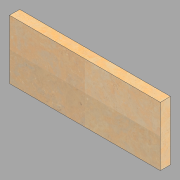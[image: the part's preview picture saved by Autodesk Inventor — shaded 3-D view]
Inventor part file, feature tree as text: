
AUTODESK INVENTOR PART (.ipt)
format: ipt  version: 2022.1 (Build 261234020, 234B)  size: 108,544 bytes
history: native  units: in
note: dims shown in document units (in); Inventor stores cm internally (conversion verified against a paired STEP export)
features: extrude x1, sketch x1
ambient origin geometry x8: Origin, YZ Plane, XZ Plane, XY Plane, X Axis, Y Axis, Z Axis, Center Point
bodies: Solid1 (feature_tree)
feature tree (2):
  extrude  "Extrusion1"  Depth=11.625in
  sketch  "Sketch1"  dims[d0=29.625in d1=11.625in d2=2.0in d3=0.0in]
